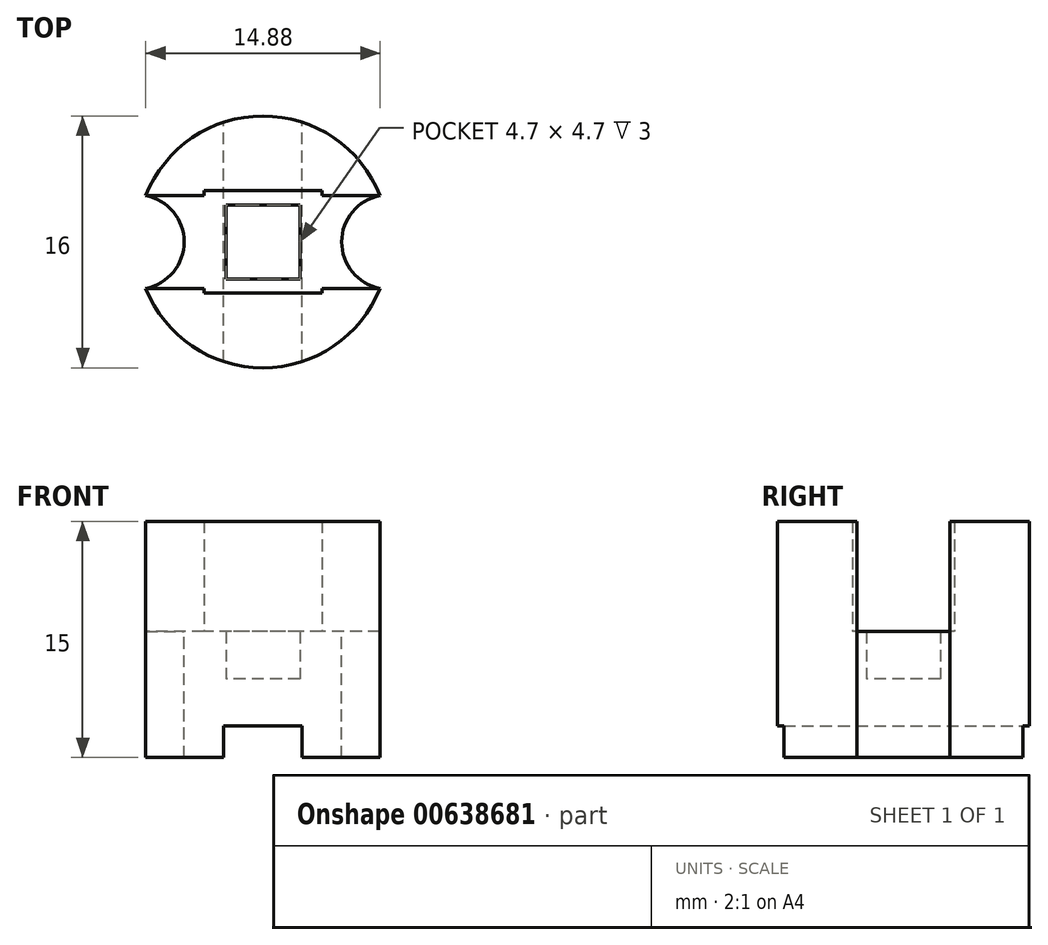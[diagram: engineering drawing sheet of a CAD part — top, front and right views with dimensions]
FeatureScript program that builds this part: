
annotation { "Feature Type Name" : "Feature", "Feature Type Description" : "" }
export const myFeature = defineFeature(function(context is Context, id is Id, definition is map)
    precondition{}
    {
        {
            var Q0;
            Q0=qCreatedBy(makeId("Top.planeOp"),FACE);
            var sketch = newSketch(context, id + "F0", { "sketchPlane" : qUnion([Q0])});
            skCircle(sketch, "E0", {"center": v(0, 0) * mm, "radius": 8 * mm});
            skSolve(sketch);
        }
        {
            var Q0;
            Q0 = qSketchRegion(id + "F0", true);
            extrude(context, id + "F1", {"entities" : qUnion([Q0]), "depth" : 3 * mm, "offsetDistance" : 25 * mm});
        }
        {
            var Q0;
            Q0=makeQuery(id+"F1.opExtrude","CAP_FACE",FACE,{"disambiguationData":[OSD([sQuery(id+"F0.wireOp",EDGE,"E0")])],"isStart":true});
            var sketch = newSketch(context, id + "F2", { "sketchPlane" : qUnion([Q0])});
            skArc(sketch, "E1.0", {"start": v(-2.5, 7.6) * mm, "mid": v(-8, 0) * mm, "end": v(-2.5, -7.6) * mm});
            skLineSegment(sketch, "E2.left", {"start": v(2.5, 7.6) * mm, "end": v(2.5, -7.6) * mm});
            skLineSegment(sketch, "E2.right", {"start": v(-2.5, 7.6) * mm, "end": v(-2.5, -7.6) * mm});
            skPoint(sketch, "E2.bottom.end.orphan", {"position": v(-2.5, 11.52) * mm});
            skPoint(sketch, "E3.orphan", {"position": v(2.5, 11.52) * mm});
            skArc(sketch, "E4.trimOffspring", {"start": v(2.5, -7.6) * mm, "mid": v(8, 0) * mm, "end": v(2.5, 7.6) * mm});
            skPoint(sketch, "E2.top.end.orphan", {"position": v(-2.5, -11.52) * mm});
            skPoint(sketch, "E5.orphan", {"position": v(2.5, -11.52) * mm});
            skSolve(sketch);
        }
        {
            var Q0;
            Q0 = qSketchRegion(id + "F2", true);
            extrude(context, id + "F3", {"entities" : qUnion([Q0]), "operationType" : NewBodyOperationType.ADD, "depth" : 2 * mm, "offsetDistance" : 25 * mm});
        }
        {
            var Q0;
            Q0=makeQuery(id+"F1.opExtrude","CAP_FACE",FACE,{"disambiguationData":[OSD([sQuery(id+"F0.wireOp",EDGE,"E0")])],"isStart":false});
            var sketch = newSketch(context, id + "F4", { "sketchPlane" : qUnion([Q0])});
            skCircle(sketch, "E6", {"center": v(-8, 0) * mm, "radius": 3 * mm});
            skLineSegment(sketch, "E7", {"start": v(0, 0) * mm, "end": v(0, 11.3) * mm, "construction": true});
            skCircle(sketch, "E8.MirrorC", {"center": v(8, 0) * mm, "radius": 3 * mm});
            skSolve(sketch);
        }
        {
            var Q0;
            Q0 = qSketchRegion(id + "F4", true);
            extrude(context, id + "F5", {"entities" : qUnion([Q0]), "operationType" : NewBodyOperationType.REMOVE, "oppositeDirection" : true, "depth" : 25 * mm, "offsetDistance" : 25 * mm});
        }
        {
            var Q0;
            Q0=makeQuery(id+"F1.opExtrude","CAP_FACE",FACE,{"disambiguationData":[OSD([sQuery(id+"F0.wireOp",EDGE,"E0")])],"isStart":false});
            var sketch = newSketch(context, id + "F6", { "sketchPlane" : qUnion([Q0])});
            skLineSegment(sketch, "E9.bottom", {"start": v(3.75, 3.25) * mm, "end": v(-3.75, 3.25) * mm});
            skLineSegment(sketch, "E9.top", {"start": v(3.75, -3.25) * mm, "end": v(-3.75, -3.25) * mm});
            skLineSegment(sketch, "E9.left", {"start": v(3.75, 3.25) * mm, "end": v(3.75, 2.95) * mm});
            skLineSegment(sketch, "E9.right", {"start": v(-3.75, 3.25) * mm, "end": v(-3.75, 2.95) * mm});
            skPoint(sketch, "E9.middle", {"position": v(0, 0) * mm});
            skArc(sketch, "E10.0", {"start": v(7.44, 2.95) * mm, "mid": v(0, 8) * mm, "end": v(-7.44, 2.95) * mm});
            skArc(sketch, "E11.0", {"start": v(-7.44, -2.95) * mm, "mid": v(0, -8) * mm, "end": v(7.44, -2.95) * mm});
            skLineSegment(sketch, "E12.bottom", {"start": v(7.44, 2.95) * mm, "end": v(3.75, 2.95) * mm});
            skLineSegment(sketch, "E12.top", {"start": v(7.44, -2.95) * mm, "end": v(3.75, -2.95) * mm});
            skLineSegment(sketch, "E12.left", {"start": v(7.44, 2.95) * mm, "end": v(7.44, -2.95) * mm});
            skLineSegment(sketch, "E13.trimOffspring", {"start": v(-3.75, 2.95) * mm, "end": v(-7.44, 2.95) * mm});
            skLineSegment(sketch, "E14.trimOffspring", {"start": v(-3.75, -2.95) * mm, "end": v(-3.75, -3.25) * mm});
            skLineSegment(sketch, "E15.trimOffspring", {"start": v(-3.75, -2.95) * mm, "end": v(-7.44, -2.95) * mm});
            skLineSegment(sketch, "E16.trimOffspring", {"start": v(3.75, -2.95) * mm, "end": v(3.75, -3.25) * mm});
            skSolve(sketch);
        }
        {
            var Q0;
            Q0 = qSketchRegion(id + "F6", true);
            extrude(context, id + "F7", {"entities" : qUnion([Q0]), "operationType" : NewBodyOperationType.ADD, "depth" : 10 * mm, "offsetDistance" : 25 * mm});
        }
        {
            var Q0;
            Q0=makeQuery(id+"F1.opExtrude","CAP_FACE",FACE,{"disambiguationData":[OSD([sQuery(id+"F0.wireOp",EDGE,"E0")])],"isStart":false});
            var sketch = newSketch(context, id + "F8", { "sketchPlane" : qUnion([Q0])});
            skLineSegment(sketch, "E17.bottom", {"start": v(2.35, 2.35) * mm, "end": v(-2.35, 2.35) * mm});
            skLineSegment(sketch, "E17.top", {"start": v(2.35, -2.35) * mm, "end": v(-2.35, -2.35) * mm});
            skLineSegment(sketch, "E17.left", {"start": v(2.35, 2.35) * mm, "end": v(2.35, -2.35) * mm});
            skLineSegment(sketch, "E17.right", {"start": v(-2.35, 2.35) * mm, "end": v(-2.35, -2.35) * mm});
            skPoint(sketch, "E17.middle", {"position": v(0, 0) * mm});
            skArc(sketch, "E18.0", {"start": v(-7.44, -2.95) * mm, "mid": v(-5, 0) * mm, "end": v(-7.44, 2.95) * mm});
            skLineSegment(sketch, "E19.0", {"start": v(-3.75, 2.95) * mm, "end": v(-7.44, 2.95) * mm});
            skLineSegment(sketch, "E20.0", {"start": v(-3.75, 3.25) * mm, "end": v(-3.75, 2.95) * mm});
            skLineSegment(sketch, "E21.0", {"start": v(3.75, 3.25) * mm, "end": v(-3.75, 3.25) * mm});
            skLineSegment(sketch, "E22.0", {"start": v(3.75, 3.25) * mm, "end": v(3.75, 2.95) * mm});
            skLineSegment(sketch, "E23.0", {"start": v(7.44, 2.95) * mm, "end": v(3.75, 2.95) * mm});
            skArc(sketch, "E24.0", {"start": v(7.44, -2.95) * mm, "mid": v(5, 0) * mm, "end": v(7.44, 2.95) * mm});
            skLineSegment(sketch, "E25.0", {"start": v(7.44, -2.95) * mm, "end": v(3.75, -2.95) * mm});
            skLineSegment(sketch, "E26.0", {"start": v(3.75, -2.95) * mm, "end": v(3.75, -3.25) * mm});
            skLineSegment(sketch, "E27.0", {"start": v(3.75, -3.25) * mm, "end": v(-3.75, -3.25) * mm});
            skLineSegment(sketch, "E28.0", {"start": v(-3.75, -2.95) * mm, "end": v(-3.75, -3.25) * mm});
            skLineSegment(sketch, "E29.0", {"start": v(-3.75, -2.95) * mm, "end": v(-7.44, -2.95) * mm});
            skSolve(sketch);
        }
        {
            var Q0;
            Q0 = qSketchRegion(id + "F8", true);
            extrude(context, id + "F9", {"entities" : qUnion([Q0]), "operationType" : NewBodyOperationType.ADD, "depth" : 3 * mm, "offsetDistance" : 25 * mm});
        }
    });
